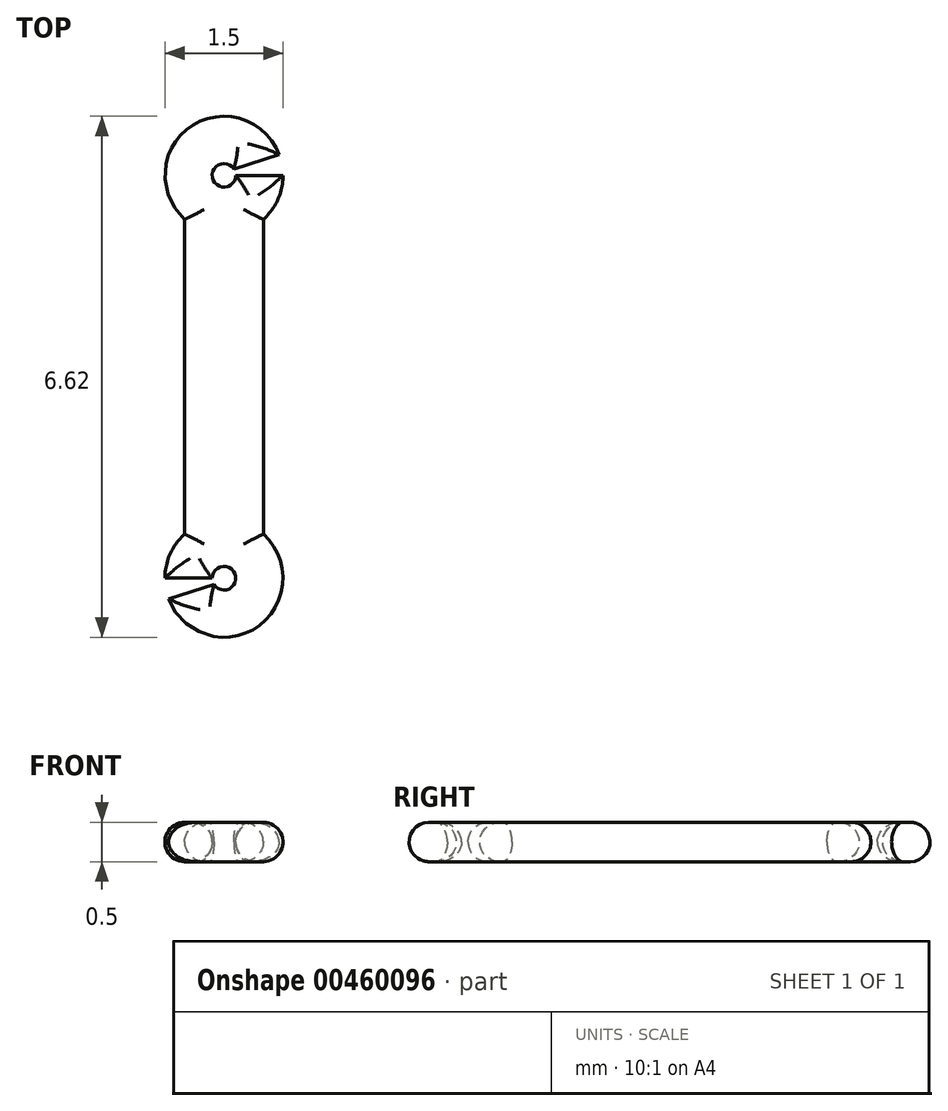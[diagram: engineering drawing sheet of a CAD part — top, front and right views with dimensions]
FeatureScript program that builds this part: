
annotation { "Feature Type Name" : "Feature", "Feature Type Description" : "" }
export const myFeature = defineFeature(function(context is Context, id is Id, definition is map)
    precondition{}
    {
        {
            var Q0;
            Q0=qCreatedBy(makeId("Top.planeOp"),FACE);
            var sketch = newSketch(context, id + "F0", { "sketchPlane" : qUnion([Q0])});
            skArc(sketch, "E0", {"start": v(0.5, 2) * mm, "mid": v(0.68, 2.25) * mm, "end": v(0.75, 2.56) * mm});
            skArc(sketch, "E1.MirrorC", {"start": v(0.5, -2) * mm, "mid": v(0.42, -3.18) * mm, "end": v(-0.7, -2.82) * mm});
            skLineSegment(sketch, "E2", {"start": v(0.5, 2) * mm, "end": v(0.5, -2) * mm});
            skLineSegment(sketch, "E3.MirrorCS", {"start": v(-0.5, 2) * mm, "end": v(-0.5, -2) * mm});
            skArc(sketch, "E4", {"start": v(-0.13, -2.64) * mm, "mid": v(0.14, -2.52) * mm, "end": v(-0.15, -2.56) * mm});
            skArc(sketch, "E5.MirrorC", {"start": v(0.15, 2.56) * mm, "mid": v(-0.14, 2.52) * mm, "end": v(0.13, 2.64) * mm});
            skLineSegment(sketch, "E6", {"start": v(0.15, 2.56) * mm, "end": v(0.75, 2.56) * mm});
            skLineSegment(sketch, "E7", {"start": v(0.7, 2.82) * mm, "end": v(0.13, 2.64) * mm});
            skLineSegment(sketch, "E8.MirrorCS", {"start": v(-0.15, -2.56) * mm, "end": v(-0.75, -2.56) * mm});
            skLineSegment(sketch, "E9.MirrorCS", {"start": v(-0.7, -2.82) * mm, "end": v(-0.13, -2.64) * mm});
            skArc(sketch, "E10.trimOffspring", {"start": v(0.7, 2.82) * mm, "mid": v(-0.42, 3.18) * mm, "end": v(-0.5, 2) * mm});
            skArc(sketch, "E11.trimOffspring", {"start": v(-0.75, -2.56) * mm, "mid": v(-0.68, -2.25) * mm, "end": v(-0.5, -2) * mm});
            skSolve(sketch);
        }
        {
            var Q0;
            Q0=makeQuery(id+"F0.imprint","IMPRINT",FACE,{"disambiguationData":[TD([[makeQuery(id+"F0.imprint","IMPRINT",EDGE,{"derivedFrom":sQuery(id+"F0.wireOp",EDGE,"E0")}),1.0]])]});
            extrude(context, id + "F1", {"entities" : qUnion([Q0]), "depth" : 0.5 * mm});
        }
        {
            var Q0;
            Q0=makeQuery(id+"F1.opExtrude","CAP_FACE",FACE,{"disambiguationData":[OSD([sQuery(id+"F0.wireOp",EDGE,"E0"),sQuery(id+"F0.wireOp",EDGE,"E1.MirrorC"),sQuery(id+"F0.wireOp",EDGE,"E2"),sQuery(id+"F0.wireOp",EDGE,"E3.MirrorCS"),sQuery(id+"F0.wireOp",EDGE,"E4"),sQuery(id+"F0.wireOp",EDGE,"E5.MirrorC"),sQuery(id+"F0.wireOp",EDGE,"E6"),sQuery(id+"F0.wireOp",EDGE,"E7"),sQuery(id+"F0.wireOp",EDGE,"E8.MirrorCS"),sQuery(id+"F0.wireOp",EDGE,"E9.MirrorCS"),sQuery(id+"F0.wireOp",EDGE,"E10.trimOffspring"),sQuery(id+"F0.wireOp",EDGE,"E11.trimOffspring")])],"isStart":false});
            fillet(context, id + "F2", {"entities" : qUnion([Q0]), "radius" : 0.25 * mm, "tangentPropagation" : true, "allowEdgeOverflow" : false});
        }
        {
            var Q0;
            Q0=makeQuery(id+"F1.opExtrude","CAP_FACE",FACE,{"disambiguationData":[OSD([sQuery(id+"F0.wireOp",EDGE,"E0"),sQuery(id+"F0.wireOp",EDGE,"E1.MirrorC"),sQuery(id+"F0.wireOp",EDGE,"E2"),sQuery(id+"F0.wireOp",EDGE,"E3.MirrorCS"),sQuery(id+"F0.wireOp",EDGE,"E4"),sQuery(id+"F0.wireOp",EDGE,"E5.MirrorC"),sQuery(id+"F0.wireOp",EDGE,"E6"),sQuery(id+"F0.wireOp",EDGE,"E7"),sQuery(id+"F0.wireOp",EDGE,"E8.MirrorCS"),sQuery(id+"F0.wireOp",EDGE,"E9.MirrorCS"),sQuery(id+"F0.wireOp",EDGE,"E10.trimOffspring"),sQuery(id+"F0.wireOp",EDGE,"E11.trimOffspring")])],"isStart":true});
            fillet(context, id + "F3", {"entities" : qUnion([Q0]), "radius" : 0.25 * mm, "tangentPropagation" : true, "allowEdgeOverflow" : false});
        }
    });
